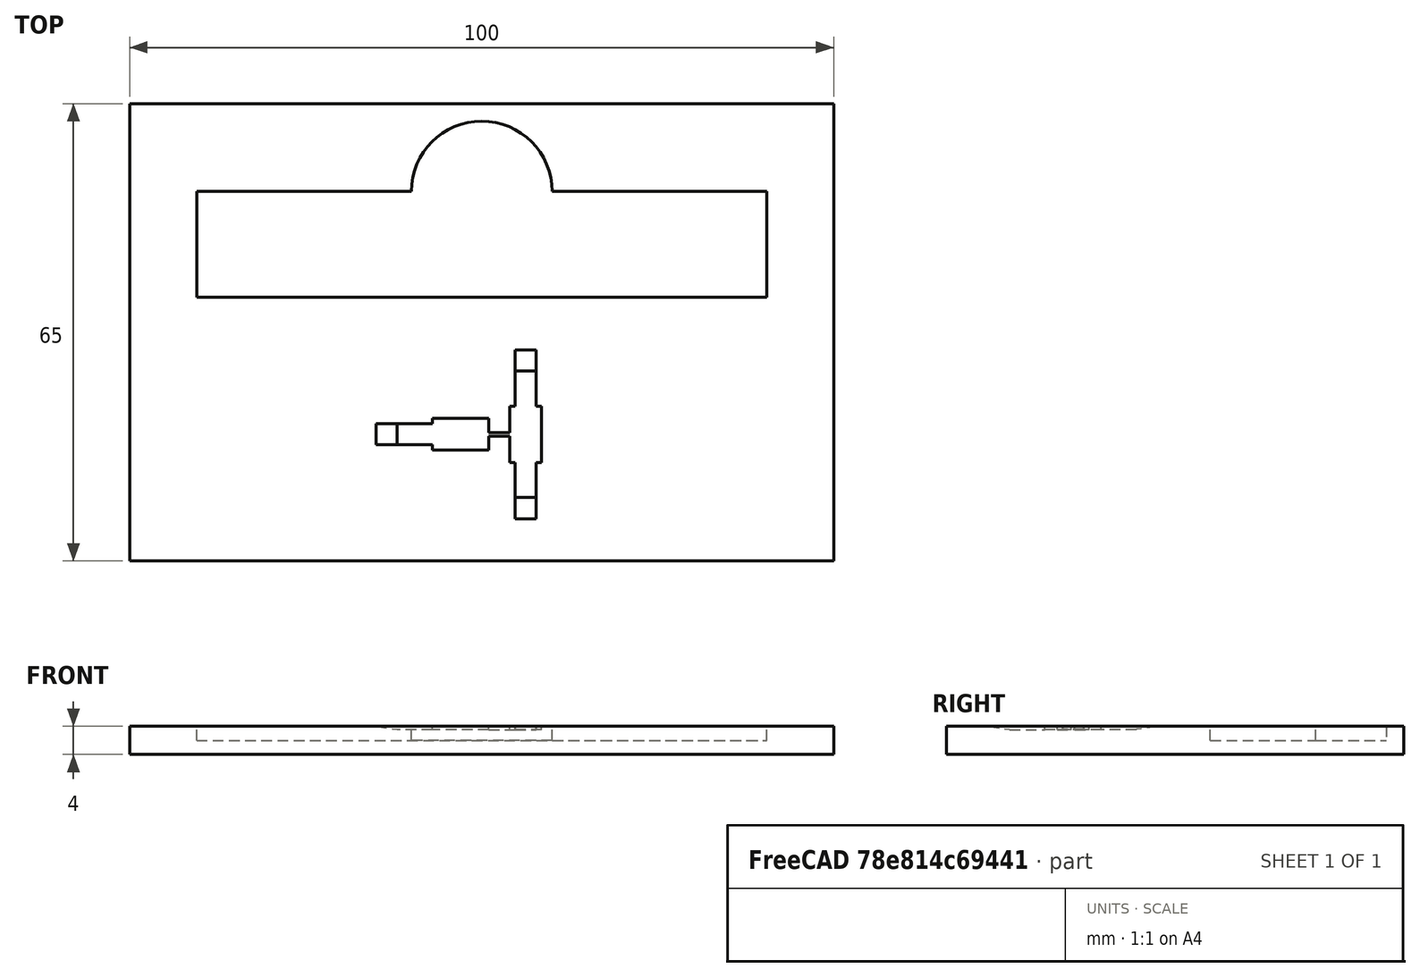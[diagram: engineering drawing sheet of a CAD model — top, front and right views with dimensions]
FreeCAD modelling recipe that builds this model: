
FCSTD DOCUMENT  (FreeCAD 1.0R39285 (Git))
Label: build_plate
License: All rights reserved
LicenseURL: https://en.wikipedia.org/wiki/All_rights_reserved
objects: Sketcher::SketchObject×3, PartDesign::Pad×3, PartDesign::Body×3, Part::Cut×2, Mesh::Feature×1, Part::Chamfer×1
note: 21 computed .brp shape members not serialized (recipe doc carries the construction recipe); baked Part::Feature solids carry a one-line shape summary decoded from their .brp

FEATURE [Mesh::Feature] load_cell
  Placement = pos=(0,0,-6.9) rot=(0,0,1;3.14159rad)
FEATURE [Sketcher::SketchObject] Sketch
  ArcFitTolerance = 1e-06
  AttachmentSupport = -> [XY_Plane]
  FullyConstrained = true
  MakeInternals = false
  MapMode = 5
  sketch-geometry (4):
    g0: LineSegment StartX=-50 StartY=20 StartZ=0 EndX=-50 EndY=-45 EndZ=0
    g1: LineSegment StartX=-50 StartY=-45 StartZ=0 EndX=50 EndY=-45 EndZ=0
    g2: LineSegment StartX=50 StartY=-45 StartZ=0 EndX=50 EndY=20 EndZ=0
    g3: LineSegment StartX=50 StartY=20 StartZ=0 EndX=-50 EndY=20 EndZ=0
  constraints (11):
    c: Coincident(g0,g1)
    c: Coincident(g1,g2)
    c: Coincident(g2,g3)
    c: Coincident(g3,g0)
    c: Vertical(g0)
    c: Vertical(g2)
    c: Horizontal(g1)
    c: DistanceX(g3,g3) = 100
    c: Symmetric(g0,g2,g-2)
    c: DistanceY(g-1,g2) = 20
    c: DistanceY(g2,g2) = 65
FEATURE [PartDesign::Pad] Pad
  Direction = (0,0,1)
  Length = 4
  Length2 = 10
  Profile = -> Sketch
  ReferenceAxis = -> Sketch [N_Axis]
  Refine = true
  Suppressed = false
  Type = 0
FEATURE [PartDesign::Body] Body  label="Base"
  AllowCompound = false
  Group = -> [Sketch,Pad]
  Origin = -> Origin
  Tip = -> Pad
FEATURE [Sketcher::SketchObject] Sketch001
  ArcFitTolerance = 1e-06
  AttachmentOffset = pos=(0,0,2) rot=(0,0,1;0rad)
  AttachmentSupport = -> [XY_Plane001]
  FullyConstrained = true
  MakeInternals = false
  MapMode = 5
  Placement = pos=(0,0,2) rot=(0,0,1;0rad)
  sketch-geometry (7):
    g0: LineSegment StartX=-40.5 StartY=7.5 StartZ=0 EndX=-40.5 EndY=-7.5 EndZ=0
    g1: LineSegment StartX=-40.5 StartY=-7.5 StartZ=0 EndX=40.5 EndY=-7.5 EndZ=0
    g2: LineSegment StartX=40.5 StartY=-7.5 StartZ=0 EndX=40.5 EndY=7.5 EndZ=0
    g3: LineSegment [constr] StartX=40.5 StartY=7.5 StartZ=0 EndX=-40.5 EndY=7.5 EndZ=0
    g4: ArcOfCircle CenterX=1.3e-15 CenterY=7.5 CenterZ=0 NormalX=0 NormalY=0 NormalZ=1 AngleXU=0 Radius=10 StartAngle=0 EndAngle=3.14159
    g5: LineSegment StartX=-40.5 StartY=7.5 StartZ=0 EndX=-10 EndY=7.5 EndZ=0
    g6: LineSegment StartX=10 StartY=7.5 StartZ=0 EndX=40.5 EndY=7.5 EndZ=0
  constraints (19):
    c: Coincident(g0,g1)
    c: Coincident(g1,g2)
    c: Coincident(g2,g3)
    c: Coincident(g3,g0)
    c: Vertical(g0)
    c: Vertical(g2)
    c: Horizontal(g1)
    c: Horizontal(g3)
    c: Symmetric(g0,g1,g-1)
    c: DistanceX(g3,g3) = 81
    c: DistanceY(g2,g2) = 15
    c: Symmetric(g3,g3,g4)
    c: PointOnObject(g4,g3)
    c: PointOnObject(g4,g3)
    c: Diameter(g4) = 20
    c: Coincident(g5,g0)
    c: Coincident(g5,g4)
    c: Coincident(g6,g4)
    c: Coincident(g6,g2)
FEATURE [PartDesign::Pad] Pad001
  Direction = (0,0,1)
  Length = 2
  Length2 = 10
  Profile = -> Sketch001
  ReferenceAxis = -> Sketch001 [N_Axis]
  Refine = true
  Suppressed = false
  Type = 0
FEATURE [PartDesign::Body] Body001  label="LoadCellFrame"
  AllowCompound = false
  Group = -> [Sketch001,Pad001]
  Origin = -> Origin001
  Tip = -> Pad001
FEATURE [Part::Cut] Cut
  Base = -> Body
  Refine = true
  Tool = -> Body001
FEATURE [Sketcher::SketchObject] Sketch002
  ArcFitTolerance = 1e-06
  AttachmentOffset = pos=(0,-27,3.5) rot=(0,0,1;0rad)
  AttachmentSupport = -> [XY_Plane002]
  FullyConstrained = true
  MakeInternals = false
  MapMode = 5
  Placement = pos=(0,-27,3.5) rot=(0,0,1;0rad)
  sketch-geometry (44):
    g0: LineSegment [constr] StartX=8.5 StartY=4 StartZ=0 EndX=4 EndY=4 EndZ=0
    g1: LineSegment [constr] StartX=4 StartY=4 StartZ=0 EndX=4 EndY=-4 EndZ=0
    g2: LineSegment [constr] StartX=4 StartY=-4 StartZ=0 EndX=8.5 EndY=-4 EndZ=0
    g3: LineSegment [constr] StartX=8.5 StartY=-4 StartZ=0 EndX=8.5 EndY=4 EndZ=0
    g4: LineSegment [constr] StartX=1 StartY=2.25 StartZ=0 EndX=-7 EndY=2.25 EndZ=0
    g5: LineSegment [constr] StartX=-7 StartY=2.25 StartZ=0 EndX=-7 EndY=-2.25 EndZ=0
    g6: LineSegment [constr] StartX=-7 StartY=-2.25 StartZ=0 EndX=1 EndY=-2.25 EndZ=0
    g7: LineSegment [constr] StartX=1 StartY=-2.25 StartZ=0 EndX=1 EndY=2.25 EndZ=0
    g8: LineSegment StartX=8.5 StartY=4 StartZ=0 EndX=8.5 EndY=-4 EndZ=0
    g9: LineSegment StartX=1 StartY=2.25 StartZ=0 EndX=-7 EndY=2.25 EndZ=0
    g10: LineSegment StartX=-7 StartY=-2.25 StartZ=0 EndX=1 EndY=-2.25 EndZ=0
    g11: LineSegment StartX=8.5 StartY=-4 StartZ=0 EndX=7.75 EndY=-4 EndZ=0
    g12: LineSegment StartX=4 StartY=-4 StartZ=0 EndX=4.75 EndY=-4 EndZ=0
    g13: LineSegment StartX=4 StartY=4 StartZ=0 EndX=4.75 EndY=4 EndZ=0
    g14: LineSegment StartX=8.5 StartY=4 StartZ=0 EndX=7.75 EndY=4 EndZ=0
    g15: LineSegment StartX=-7 StartY=2.25 StartZ=0 EndX=-7 EndY=1.5 EndZ=0
    g16: LineSegment StartX=-7 StartY=-2.25 StartZ=0 EndX=-7 EndY=-1.5 EndZ=0
    g17: LineSegment [constr] StartX=7.75 StartY=-4 StartZ=0 EndX=4.75 EndY=-4 EndZ=0
    g18: LineSegment [constr] StartX=4.75 StartY=-4 StartZ=0 EndX=4.75 EndY=-9 EndZ=0
    g19: LineSegment [constr] StartX=4.75 StartY=-9 StartZ=0 EndX=7.75 EndY=-9 EndZ=0
    g20: LineSegment [constr] StartX=7.75 StartY=-9 StartZ=0 EndX=7.75 EndY=-4 EndZ=0
    g21: LineSegment [constr] StartX=7.75 StartY=4 StartZ=0 EndX=7.75 EndY=9 EndZ=0
    g22: LineSegment [constr] StartX=7.75 StartY=9 StartZ=0 EndX=4.75 EndY=9 EndZ=0
    g23: LineSegment [constr] StartX=4.75 StartY=9 StartZ=0 EndX=4.75 EndY=4 EndZ=0
    g24: LineSegment [constr] StartX=4.75 StartY=4 StartZ=0 EndX=7.75 EndY=4 EndZ=0
    g25: LineSegment [constr] StartX=-7 StartY=1.5 StartZ=0 EndX=-12 EndY=1.5 EndZ=0
    g26: LineSegment [constr] StartX=-12 StartY=1.5 StartZ=0 EndX=-12 EndY=-1.5 EndZ=0
    g27: LineSegment [constr] StartX=-12 StartY=-1.5 StartZ=0 EndX=-7 EndY=-1.5 EndZ=0
    g28: LineSegment [constr] StartX=-7 StartY=-1.5 StartZ=0 EndX=-7 EndY=1.5 EndZ=0
    g29: LineSegment StartX=7.75 StartY=9 StartZ=0 EndX=7.75 EndY=4 EndZ=0
    g30: LineSegment StartX=4.75 StartY=9 StartZ=0 EndX=4.75 EndY=4 EndZ=0
    g31: LineSegment StartX=4.75 StartY=9 StartZ=0 EndX=7.75 EndY=9 EndZ=0
    g32: LineSegment StartX=7.75 StartY=-4 StartZ=0 EndX=7.75 EndY=-9 EndZ=0
    g33: LineSegment StartX=7.75 StartY=-9 StartZ=0 EndX=4.75 EndY=-9 EndZ=0
    g34: LineSegment StartX=4.75 StartY=-9 StartZ=0 EndX=4.75 EndY=-4 EndZ=0
    g35: LineSegment StartX=-7 StartY=1.5 StartZ=0 EndX=-12 EndY=1.5 EndZ=0
    g36: LineSegment StartX=-12 StartY=1.5 StartZ=0 EndX=-12 EndY=-1.5 EndZ=0
    g37: LineSegment StartX=-12 StartY=-1.5 StartZ=0 EndX=-7 EndY=-1.5 EndZ=0
    g38: LineSegment StartX=1 StartY=0.25 StartZ=0 EndX=4 EndY=0.25 EndZ=0
    g39: LineSegment StartX=1 StartY=-0.25 StartZ=0 EndX=4 EndY=-0.25 EndZ=0
    g40: LineSegment StartX=1 StartY=-2.25 StartZ=0 EndX=1 EndY=-0.25 EndZ=0
    g41: LineSegment StartX=1 StartY=0.25 StartZ=0 EndX=1 EndY=2.25 EndZ=0
    g42: LineSegment StartX=4 StartY=4 StartZ=0 EndX=4 EndY=0.25 EndZ=0
    g43: LineSegment StartX=4 StartY=-0.25 StartZ=0 EndX=4 EndY=-4 EndZ=0
  constraints (109):
    c: Coincident(g0,g1)
    c: Coincident(g1,g2)
    c: Coincident(g2,g3)
    c: Coincident(g3,g0)
    c: Horizontal(g0)
    c: Horizontal(g2)
    c: Vertical(g1)
    c: Symmetric(g0,g2,g-1)
    c: DistanceX(g0,g0) = 4.5
    c: DistanceY(g1,g1) = 8
    c: Coincident(g4,g5)
    c: Coincident(g5,g6)
    c: Coincident(g6,g7)
    c: Coincident(g7,g4)
    c: Horizontal(g4)
    c: Horizontal(g6)
    c: Vertical(g7)
    c: Symmetric(g4,g5,g-1)
    c: DistanceX(g4,g0) = 3
    c: Equal(g5,g0)
    c: Equal(g4,g1)
    c: Coincident(g8,g0)
    c: Coincident(g8,g2)
    c: Coincident(g9,g4)
    c: Coincident(g9,g4)
    c: Coincident(g10,g5)
    c: Coincident(g10,g6)
    c: Coincident(g11,g2)
    c: PointOnObject(g11,g2)
    c: Coincident(g12,g1)
    c: PointOnObject(g12,g2)
    c: Coincident(g13,g0)
    c: PointOnObject(g13,g0)
    c: Coincident(g14,g0)
    c: PointOnObject(g14,g0)
    c: Coincident(g15,g4)
    c: PointOnObject(g15,g5)
    c: Coincident(g16,g5)
    c: PointOnObject(g16,g5)
    c: Equal(g16,g15)
    c: Equal(g15,g12)
    c: Equal(g12,g11)
    c: Equal(g11,g14)
    c: Equal(g14,g13)
    c: DistanceX(g-1,g0) = 4
    c: DistanceX(g14,g14) = 0.75
    c: Coincident(g17,g18)
    c: Coincident(g18,g19)
    c: Coincident(g19,g20)
    c: Coincident(g20,g17)
    c: Horizontal(g19)
    c: Vertical(g18)
    c: Vertical(g20)
    c: Coincident(g17,g11)
    c: Coincident(g17,g12)
    c: Coincident(g21,g22)
    c: Coincident(g22,g23)
    c: Coincident(g23,g24)
    c: Coincident(g24,g21)
    c: Vertical(g21)
    c: Vertical(g23)
    c: Horizontal(g22)
    c: Coincident(g21,g14)
    c: Coincident(g23,g13)
    c: Coincident(g25,g26)
    c: Coincident(g26,g27)
    c: Coincident(g27,g28)
    c: Coincident(g28,g25)
    c: Horizontal(g25)
    c: Horizontal(g27)
    c: Vertical(g26)
    c: Coincident(g25,g15)
    c: Coincident(g27,g16)
    c: Equal(g20,g21)
    c: Equal(g21,g25)
    c: DistanceY(g21,g21) = 5
    c: Coincident(g29,g21)
    c: Coincident(g29,g14)
    c: Coincident(g30,g22)
    c: Coincident(g30,g13)
    c: Coincident(g31,g22)
    c: Coincident(g31,g21)
    c: Coincident(g32,g11)
    c: Coincident(g32,g19)
    c: Coincident(g33,g19)
    c: Coincident(g33,g18)
    c: Coincident(g34,g18)
    c: Coincident(g34,g12)
    c: Coincident(g35,g15)
    c: Coincident(g35,g25)
    c: Coincident(g36,g25)
    c: Coincident(g36,g26)
    c: Coincident(g37,g26)
    c: Coincident(g37,g16)
    c: PointOnObject(g38,g7)
    c: PointOnObject(g38,g1)
    c: Horizontal(g38)
    c: PointOnObject(g39,g1)
    c: Horizontal(g39)
    c: Coincident(g40,g6)
    c: Coincident(g40,g39)
    c: Coincident(g41,g38)
    c: Coincident(g41,g4)
    c: Coincident(g42,g0)
    c: Coincident(g42,g38)
    c: Coincident(g43,g39)
    c: Coincident(g43,g1)
    c: Symmetric(g39,g38,g-1)
    c: DistanceY(g40,g40) = 2
FEATURE [PartDesign::Pad] Pad002
  Direction = (0,0,1)
  Length = 0.5
  Length2 = 10
  Profile = -> Sketch002
  ReferenceAxis = -> Sketch002 [N_Axis]
  Refine = true
  Suppressed = false
  Type = 0
FEATURE [PartDesign::Body] Body002  label="Body"
  AllowCompound = false
  Group = -> [Sketch002,Pad002]
  Origin = -> Origin002
  Tip = -> Pad002
FEATURE [Part::Cut] Cut001
  Base = -> Cut
  Refine = true
  Tool = -> Body002
FEATURE [Part::Chamfer] Chamfer
  Base = -> Cut001
  EdgeLinks = -> Cut001 [Edge21,Edge30,Edge36]
  Edges = 3 edges: [Edge21 r1=3 r2=0.45,Edge30 r1=3 r2=0.45,Edge36 r1=3 r2=0.45]
